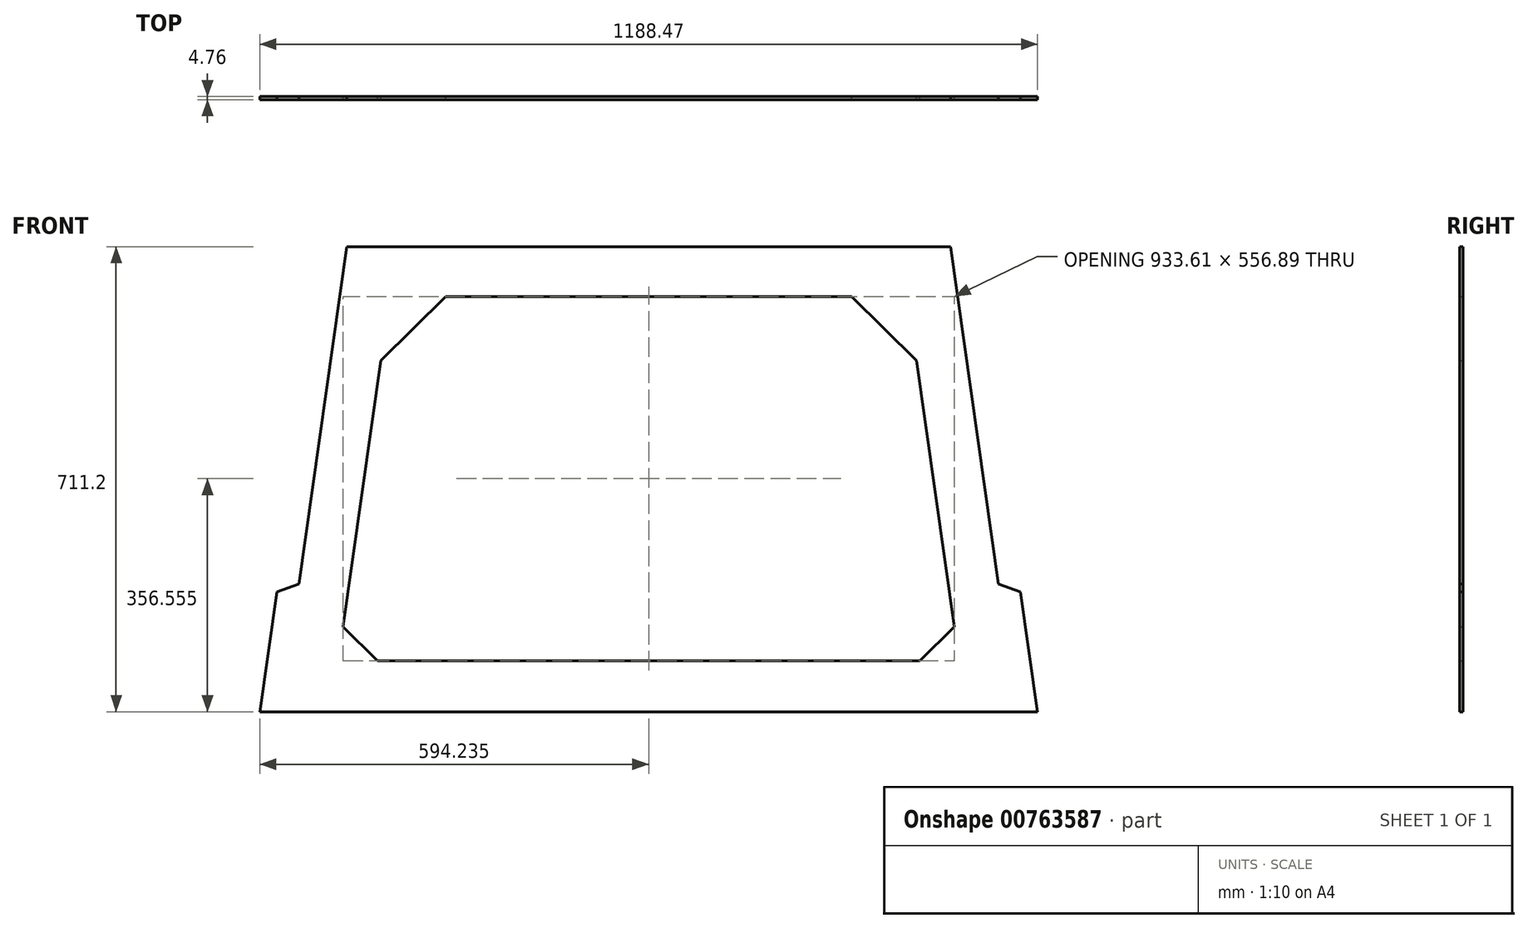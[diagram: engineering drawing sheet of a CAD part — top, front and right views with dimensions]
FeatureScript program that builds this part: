
annotation { "Feature Type Name" : "Feature", "Feature Type Description" : "" }
export const myFeature = defineFeature(function(context is Context, id is Id, definition is map)
    precondition{}
    {
        {
            var Q0;
            Q0=qCreatedBy(makeId("Front.planeOp"),FACE);
            var sketch = newSketch(context, id + "F0", { "sketchPlane" : qUnion([Q0])});
            skLineSegment(sketch, "E0.MirrorCS", {"start": v(450.82, -85.84) * mm, "end": v(476.81, -269.26) * mm});
            skLineSegment(sketch, "E1.MirrorCS", {"start": v(476.81, -269.26) * mm, "end": v(-711.66, -269.26) * mm});
            skLineSegment(sketch, "E2.MirrorCS", {"start": v(-584.23, -139.4) * mm, "end": v(-531.91, -191.15) * mm});
            skLineSegment(sketch, "E3.MirrorCS", {"start": v(297.06, -191.15) * mm, "end": v(-531.91, -191.15) * mm});
            skLineSegment(sketch, "E4.MirrorCS", {"start": v(349.38, -139.4) * mm, "end": v(297.06, -191.15) * mm});
            skLineSegment(sketch, "E5.MirrorCS", {"start": v(291.69, 267.7) * mm, "end": v(349.38, -139.4) * mm});
            skLineSegment(sketch, "E6.MirrorCS", {"start": v(192.6, 365.74) * mm, "end": v(291.69, 267.7) * mm});
            skLineSegment(sketch, "E7.MirrorCS", {"start": v(192.6, 365.74) * mm, "end": v(-427.45, 365.74) * mm});
            skLineSegment(sketch, "E8.MirrorCS", {"start": v(-427.45, 365.74) * mm, "end": v(-526.54, 267.7) * mm});
            skLineSegment(sketch, "E9.MirrorCS", {"start": v(-526.54, 267.7) * mm, "end": v(-584.23, -139.4) * mm});
            skLineSegment(sketch, "E10.MirrorCS", {"start": v(417.05, -73.8) * mm, "end": v(450.82, -85.84) * mm});
            skLineSegment(sketch, "E11.MirrorCS", {"start": v(343.96, 441.94) * mm, "end": v(417.05, -73.8) * mm});
            skLineSegment(sketch, "E12.MirrorCS", {"start": v(343.96, 441.94) * mm, "end": v(-578.8, 441.94) * mm});
            skLineSegment(sketch, "E13.MirrorCS", {"start": v(-578.8, 441.94) * mm, "end": v(-651.9, -73.8) * mm});
            skLineSegment(sketch, "E14.MirrorCS", {"start": v(-685.67, -85.84) * mm, "end": v(-711.66, -269.26) * mm});
            skLineSegment(sketch, "E15.MirrorCS", {"start": v(-651.9, -73.8) * mm, "end": v(-685.67, -85.84) * mm});
            skSolve(sketch);
        }
        {
            var Q0;
            Q0=makeQuery(id+"F0.imprint","IMPRINT",FACE,{"disambiguationData":[TD([[makeQuery(id+"F0.imprint","IMPRINT",EDGE,{"derivedFrom":sQuery(id+"F0.wireOp",EDGE,"E0.MirrorCS")}),-1.0]])]});
            extrude(context, id + "F1", {"entities" : qUnion([Q0]), "depth" : 4.76 * mm, "offsetDistance" : 25.4 * mm});
        }
    });
